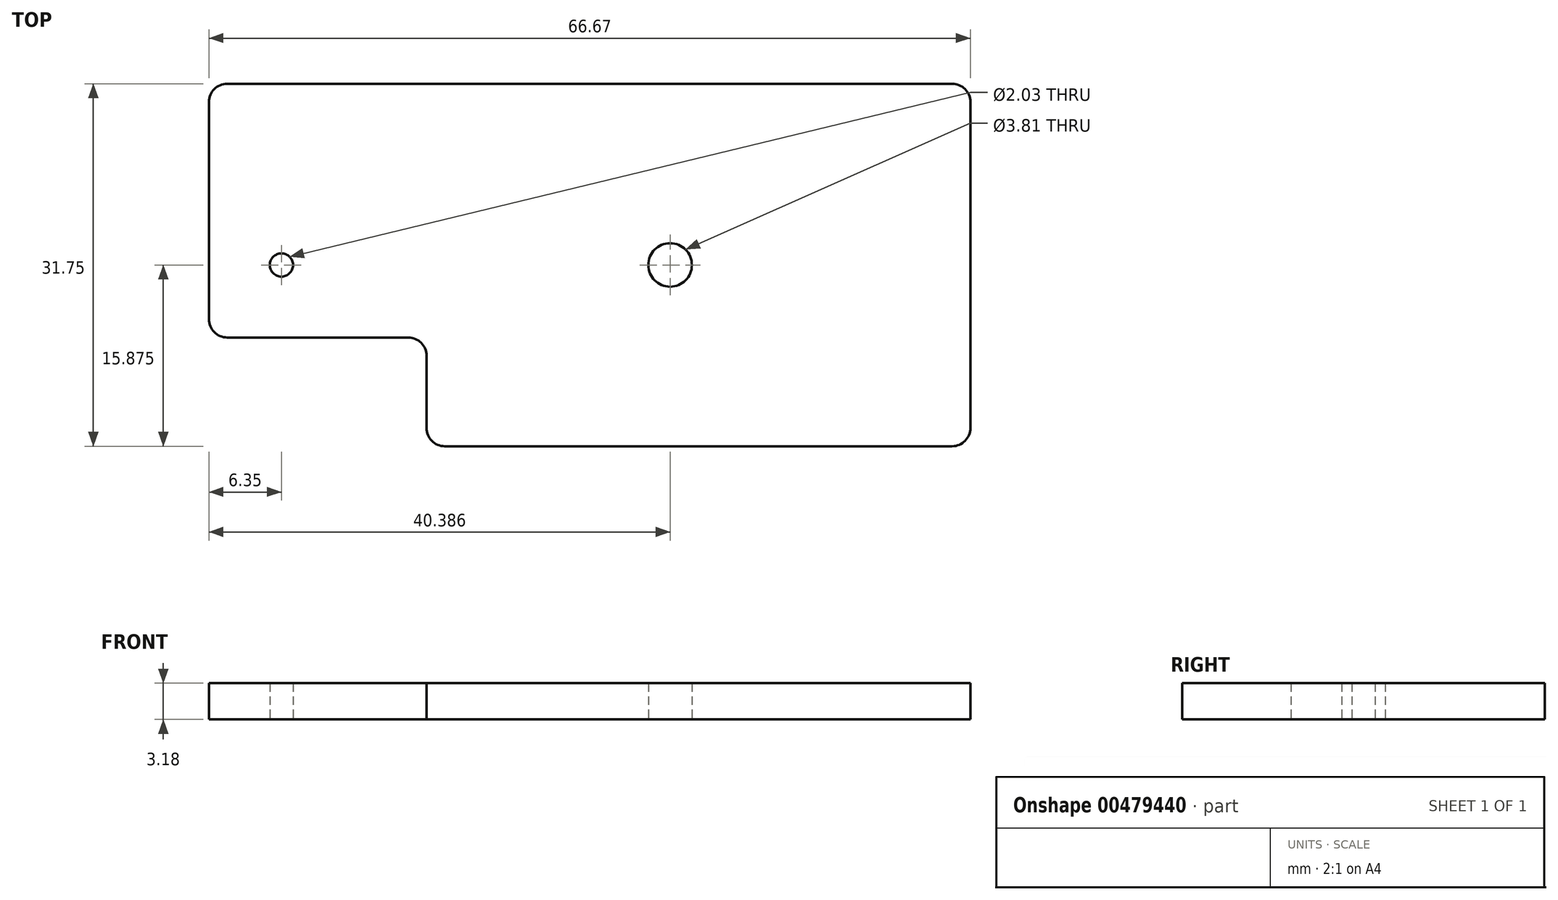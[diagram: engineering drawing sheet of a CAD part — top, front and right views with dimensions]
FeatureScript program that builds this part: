
annotation { "Feature Type Name" : "Feature", "Feature Type Description" : "" }
export const myFeature = defineFeature(function(context is Context, id is Id, definition is map)
    precondition{}
    {
        {
            var Q0;
            Q0=qCreatedBy(makeId("Top.planeOp"),FACE);
            var sketch = newSketch(context, id + "F0", { "sketchPlane" : qUnion([Q0])});
            skLineSegment(sketch, "E0.bottom", {"start": v(0, 0) * mm, "end": v(65.07, 0) * mm});
            skLineSegment(sketch, "E0.top", {"start": v(1.6, 31.75) * mm, "end": v(65.07, 31.75) * mm});
            skLineSegment(sketch, "E0.left", {"start": v(0, 0) * mm, "end": v(0, 30.15) * mm});
            skLineSegment(sketch, "E0.right", {"start": v(66.68, 1.6) * mm, "end": v(66.68, 30.15) * mm});
            skLineSegment(sketch, "E1.bottom", {"start": v(0, 0) * mm, "end": v(19.05, 0) * mm});
            skLineSegment(sketch, "E1.top", {"start": v(0, 9.53) * mm, "end": v(17.45, 9.53) * mm});
            skLineSegment(sketch, "E1.left", {"start": v(0, 0) * mm, "end": v(0, 9.53) * mm});
            skLineSegment(sketch, "E1.right", {"start": v(19.05, 0) * mm, "end": v(19.05, 7.92) * mm});
            skCircle(sketch, "E2", {"center": v(6.35, 15.88) * mm, "radius": 1.02 * mm});
            skCircle(sketch, "E3", {"center": v(40.39, 15.88) * mm, "radius": 1.9 * mm});
            skPoint(sketch, "E4.visualSharp", {"position": v(0, 31.75) * mm});
            skArc(sketch, "E4.filletArc", {"start": v(1.6, 31.75) * mm, "mid": v(0.47, 31.28) * mm, "end": v(0, 30.15) * mm});
            skPoint(sketch, "E5.visualSharp", {"position": v(66.68, 31.75) * mm});
            skArc(sketch, "E5.filletArc", {"start": v(66.68, 30.15) * mm, "mid": v(66.2, 31.28) * mm, "end": v(65.07, 31.75) * mm});
            skPoint(sketch, "E6.visualSharp", {"position": v(66.68, 0) * mm});
            skArc(sketch, "E6.filletArc", {"start": v(65.07, 0) * mm, "mid": v(66.2, 0.47) * mm, "end": v(66.68, 1.6) * mm});
            skPoint(sketch, "E7.visualSharp", {"position": v(19.05, 9.53) * mm});
            skArc(sketch, "E7.filletArc", {"start": v(19.05, 7.92) * mm, "mid": v(18.58, 9.06) * mm, "end": v(17.45, 9.53) * mm});
            skSolve(sketch);
        }
        {
            var Q0;
            Q0=makeQuery(id+"F0.imprint","IMPRINT",FACE,{"disambiguationData":[TD([[makeQuery(id+"F0.imprint","IMPRINT",EDGE,{"derivedFrom":sQuery(id+"F0.wireOp",EDGE,"E0.top")}),-1.0]])]});
            extrude(context, id + "F1", {"entities" : qUnion([Q0]), "depth" : 3.17 * mm});
        }
        {
            var Q0;
            Q0=makeQuery(id+"F1.opExtrude","SWEPT_EDGE",EDGE,{"disambiguationData":[OSD([sQuery(id+"F0.wireOp",EDGE,"E0.left"),sQuery(id+"F0.wireOp",EDGE,"E1.top")])]});
            var Q1;
            Q1=makeQuery(id+"F1.opExtrude","SWEPT_EDGE",EDGE,{"disambiguationData":[OSD([sQuery(id+"F0.wireOp",EDGE,"E0.bottom"),sQuery(id+"F0.wireOp",EDGE,"E1.right")])]});
            fillet(context, id + "F2", {"entities" : qUnion([Q0, Q1]), "radius" : 1.6 * mm, "tangentPropagation" : true, "allowEdgeOverflow" : false});
        }
    });
